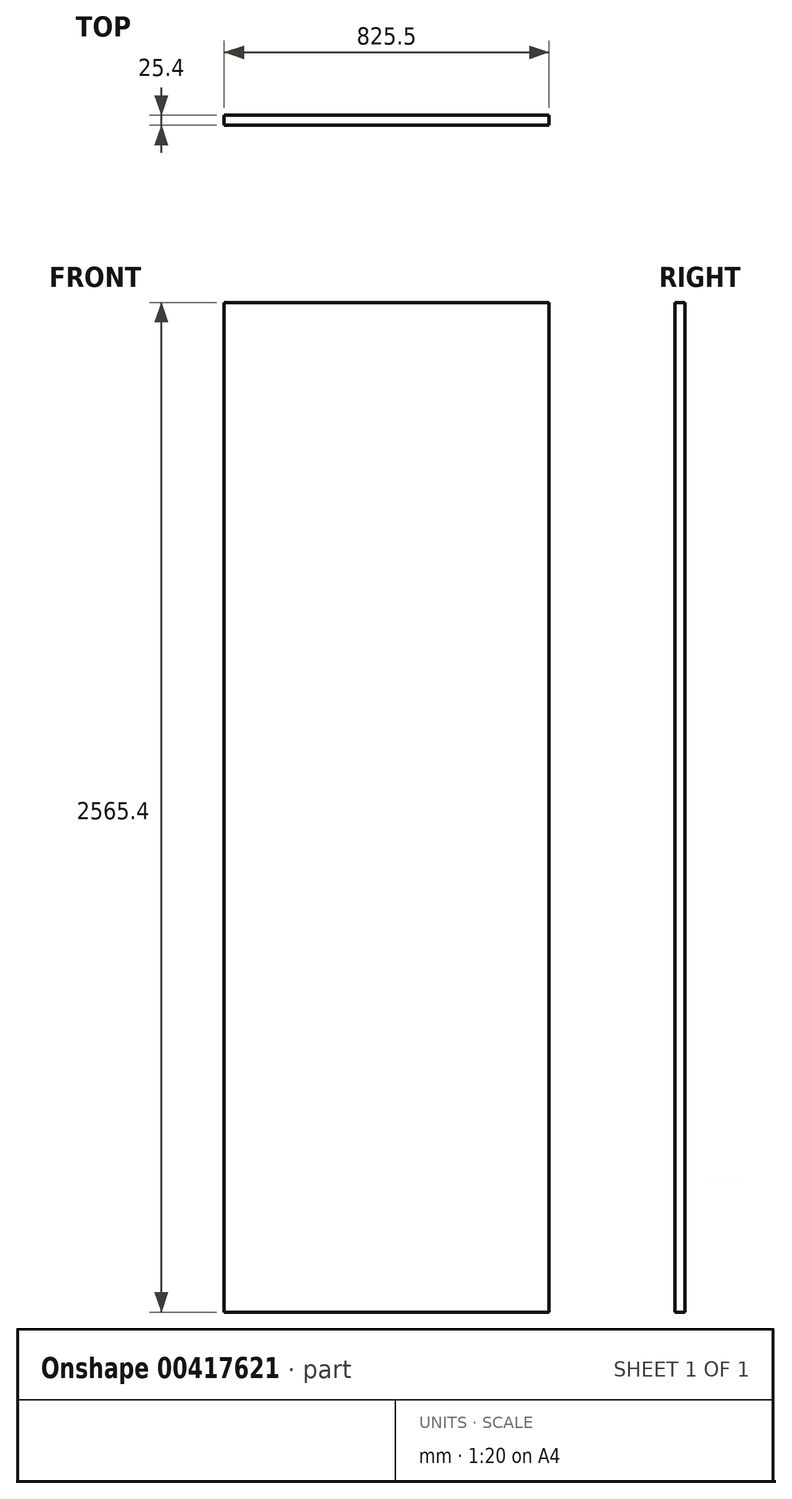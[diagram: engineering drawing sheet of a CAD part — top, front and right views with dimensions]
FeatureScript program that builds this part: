
annotation { "Feature Type Name" : "Feature", "Feature Type Description" : "" }
export const myFeature = defineFeature(function(context is Context, id is Id, definition is map)
    precondition{}
    {
        {
            var Q0;
            Q0=qCreatedBy(makeId("Front.planeOp"),FACE);
            var sketch = newSketch(context, id + "F0", { "sketchPlane" : qUnion([Q0])});
            skLineSegment(sketch, "E0.bottom", {"start": v(0, 0) * mm, "end": v(825.5, 0) * mm});
            skLineSegment(sketch, "E0.top", {"start": v(0, 2565.4) * mm, "end": v(825.5, 2565.4) * mm});
            skLineSegment(sketch, "E0.left", {"start": v(0, 0) * mm, "end": v(0, 2565.4) * mm});
            skLineSegment(sketch, "E0.right", {"start": v(825.5, 0) * mm, "end": v(825.5, 2565.4) * mm});
            skSolve(sketch);
        }
        {
            var Q0;
            Q0 = qSketchRegion(id + "F0", true);
            extrude(context, id + "F1", {"entities" : qUnion([Q0]), "oppositeDirection" : true, "depth" : 25.4 * mm});
        }
    });
